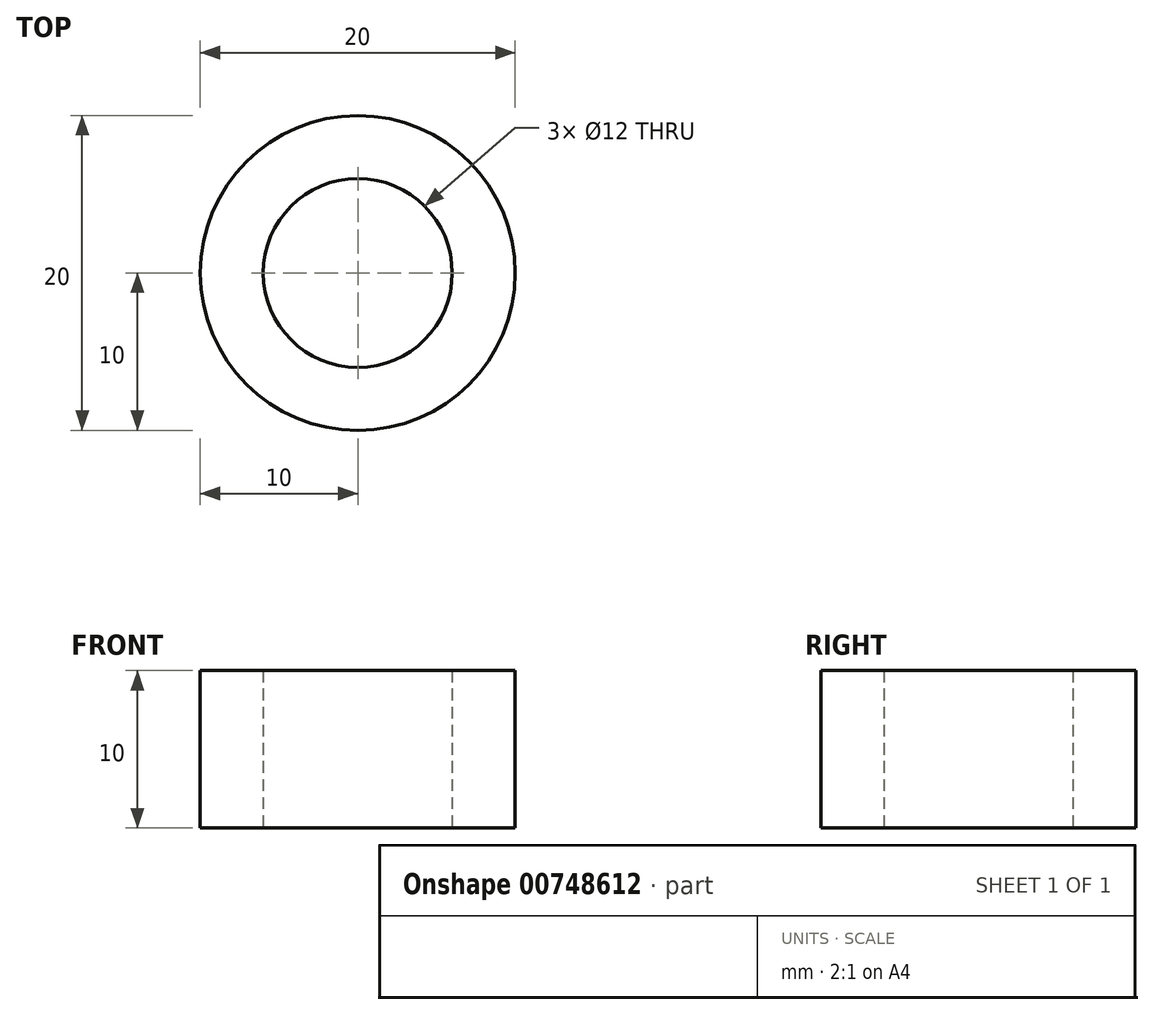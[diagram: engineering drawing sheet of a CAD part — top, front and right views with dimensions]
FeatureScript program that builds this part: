
annotation { "Feature Type Name" : "Feature", "Feature Type Description" : "" }
export const myFeature = defineFeature(function(context is Context, id is Id, definition is map)
    precondition{}
    {
        {
            var Q0;
            Q0=qCreatedBy(makeId("Top.planeOp"),FACE);
            var sketch = newSketch(context, id + "F0", { "sketchPlane" : qUnion([Q0])});
            skCircle(sketch, "E0", {"center": v(0, 0) * mm, "radius": 10 * mm});
            skCircle(sketch, "E1", {"center": v(0, 0) * mm, "radius": 6 * mm});
            skSolve(sketch);
        }
        {
            var Q0;
            Q0 = qSketchRegion(id + "F0", true);
            extrude(context, id + "F1", {"entities" : qUnion([Q0]), "depth" : 10 * mm, "offsetDistance" : 25 * mm});
        }
    });
